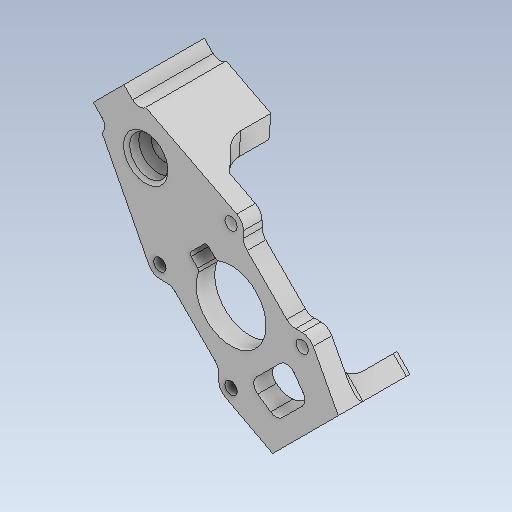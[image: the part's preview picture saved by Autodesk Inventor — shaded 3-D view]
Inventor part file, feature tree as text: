
AUTODESK INVENTOR PART (.ipt)
format: ipt  version: 2020 (Build 240168000, 168)  size: 505,344 bytes
history: native  units: mm
features: extrude x9, sketch x9, projected_geometry x9, fillet x7, thicken_offset x6, chamfer x5, other x5, reference x3, plane x2
ambient origin geometry x8: Origin, YZ Plane, XZ Plane, XY Plane, X Axis, Y Axis, Z Axis, Center Point
bodies: Solid1 (feature_tree)
feature tree (55):
  extrude  "Extrusion1"  Depth=32.0mm
  extrude  "Extrusion2"  Depth=15.0mm
  chamfer  "Chamfer1"  Distance=3.0mm
  extrude  "Extrusion3"  Depth=10.0mm TaperAngle=0.0deg
  chamfer  "Chamfer2"  Distance=2.0mm Angle=45.0deg
  fillet  "Fillet1"  Radius=19.5mm
  plane  "Work Plane1"
  plane  "Work Plane2"
  extrude  "Extrusion4"  Depth=10.0mm TaperAngle=0.0deg
  chamfer  "Chamfer3"  Distance=3.5mm Angle=45.0deg
  extrude  "Extrusion10"  [1 undecoded]
  extrude  "Extrusion11"  Depth=1.0mm
  fillet  "Fillet2"  Radius=10.0mm
  thicken_offset  "Thicken2"
  fillet  "Fillet3"  Radius=1.0mm
  fillet  "Fillet4"  Radius=8.0mm
  thicken_offset  "Thicken3"
  extrude  "Extrusion12"  Depth=2.0mm
  chamfer  "Chamfer7"  Distance=15.0mm
  fillet  "Fillet5"  Radius=10.0mm
  thicken_offset  "Thicken4"
  thicken_offset  "Thicken5"
  thicken_offset  "Thicken6"
  extrude  "Extrusion13"  Depth=4.0mm
  fillet  "Fillet8"  Radius=4.0mm
  extrude  "Extrusion14"  Depth=2.0mm TaperAngle=0.0deg
  fillet  "Fillet9"  Radius=1.5mm
  thicken_offset  "Thicken7"
  chamfer  "Chamfer10"  Distance=1.0mm
  sketch  "Sketch1"  dims[d0=6.0mm d1=32.0mm]
  reference  "Reference1"
  sketch  "Sketch2"  dims[d2=19.5mm d3=15.0mm]
  projected_geometry  "Projected Loop1"
  reference  "Reference2"
  sketch  "Sketch3"  dims[d4=15.0mm]
  projected_geometry  "Projected Loop2"
  sketch  "Sketch4"  dims[d5=10.0mm]
  projected_geometry  "Projected Loop3"
  sketch  "Sketch10"  dims[d6=10.0mm d7=3.0mm d8=0.0mm]
  projected_geometry  "Projected Loop9"
  reference  "Reference3"
  sketch  "Sketch11"  dims[d9=30.0mm d10=10.0mm d11=0.0mm d12=5.0mm d13=2.0mm d14=45.0deg d15=19.5mm]
  projected_geometry  "Projected Loop10"
  projected_geometry  "Projected Loop11"
  sketch  "Sketch12"  dims[d16=6.15mm d17=10.0mm d18=0.0mm d19=3.5mm d20=2.0mm d21=45.0deg]
  projected_geometry  "Projected Loop12"
  sketch  "Sketch13"  dims[d22=4.0mm d23=-2.0mm]
  projected_geometry  "Projected Loop13"
  sketch  "Sketch14"  dims[d24=-2.0mm d25=1.0mm d26=10.0mm d27=0.0mm d28=1.0mm d29=2.0mm d30=45.0deg d72=8.0mm d73=3.0mm d74=15.0mm d75=10.0mm d76=0.0mm d77=4.0mm d78=4.0mm d79=3.0mm d80=0.0mm d81=1.5mm d82=1.0mm d83=1.0mm d84=3.0mm d85=1.0mm d86=3.0mm d87=2.0mm d88=4.5mm d89=4.0mm d90=3.2mm d91=4.0mm d92=3.2mm d93=3.0mm d94=0.0mm d95=2.0mm d96=2.0mm d97=45.0deg d98=2.0mm d99=0.7mm d100=0.7mm d101=0.7mm d102=0.7mm d103=0.5mm d104=0.5mm d110=4.0mm d111=4.0mm d112=3.0mm d113=0.0mm d114=0.5mm d115=3.0mm d116=3.2mm d117=3.0mm d118=3.2mm d119=3.5mm d120=7.0mm d121=13.0mm d122=3.5mm d123=0.0mm d124=1.5mm d128=0.025mm d129=0.025mm d130=0.5mm d131=2.0mm d132=45.0deg d58=0.5mm d59=0.872665mm d60=0.5mm d61=0.872665mm]
  projected_geometry  "Projected Loop14"
  parser-record x1  (decoder bookkeeping rows leaked as tree rows — omitted from the tree; the rows remain in map.json)
  other  "reducer_1.iam"
  other  "mot_27_ass:1"
  other  "mot_27_2:1"
  other  "mot_27_1:1"
note: 1 required parameter value undecoded (feature->parameter linkage not recoverable at this tier; creation-order binding heuristic only, values carry confidence <= 0.55)
note: 1 file-system path scrubbed to <path> (originals preserved in map.json)
